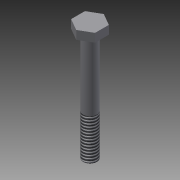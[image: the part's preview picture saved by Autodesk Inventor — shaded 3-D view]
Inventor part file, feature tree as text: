
AUTODESK INVENTOR PART (.ipt)
format: ipt  version: 2015 SP1 (Build 190203100, 203)  size: 93,184 bytes
history: native  units: in
note: dims shown in document units (in); Inventor stores cm internally (conversion verified against a paired STEP export)
features: extrude x2, sketch x2, thread x1
ambient origin geometry x8: Origin, YZ Plane, XZ Plane, XY Plane, X Axis, Y Axis, Z Axis, Center Point
bodies: Solid1 (feature_tree)
feature tree (5):
  extrude  "Extrusion1"  Depth=2.0in TaperAngle=0.0deg
  extrude  "Extrusion2"  Depth=0.4375in
  thread  "Thread1"  [1 undecoded]
  sketch  "Sketch1"  dims[d0=0.25in d1=2.0in d2=0.0in]
  sketch  "Sketch2"  dims[d3=0.4375in d4=0.4375in d5=0.4375in d6=120.0deg d7=120.0deg d8=0.2188in d9=0.2188in d10=0.2188in d11=0.1562in d12=0.0in d13=0.75in d14=1.25in]
note: 1 required parameter value undecoded (feature->parameter linkage not recoverable at this tier; creation-order binding heuristic only, values carry confidence <= 0.55)
